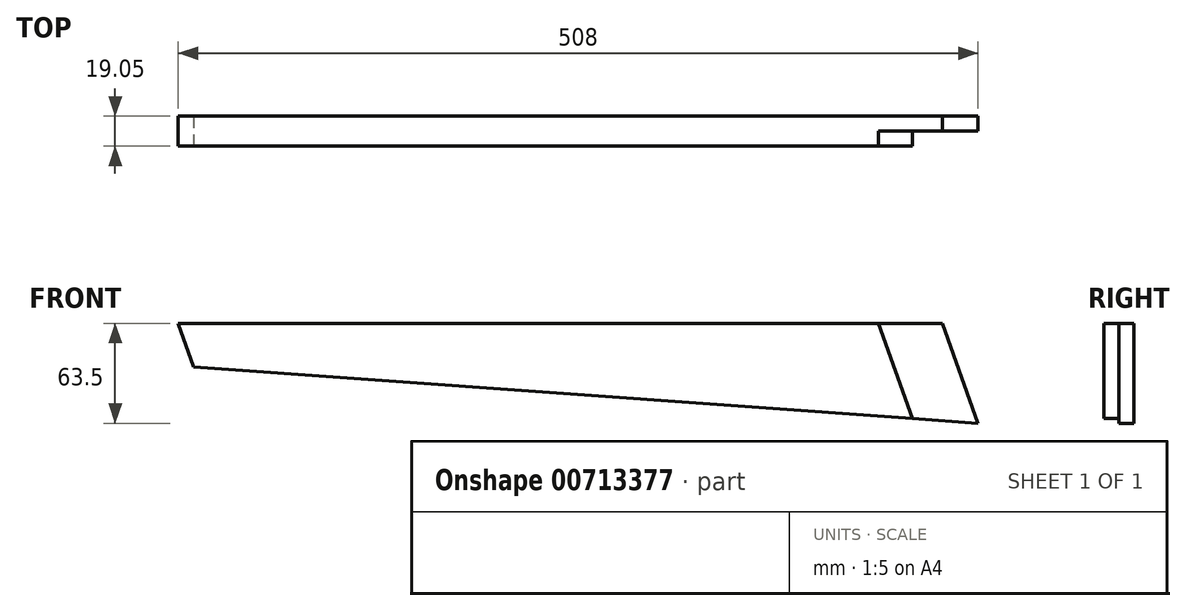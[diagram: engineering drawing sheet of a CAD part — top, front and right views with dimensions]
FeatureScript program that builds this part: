
annotation { "Feature Type Name" : "Feature", "Feature Type Description" : "" }
export const myFeature = defineFeature(function(context is Context, id is Id, definition is map)
    precondition{}
    {
        {
            var Q0;
            Q0=qCreatedBy(makeId("Front.planeOp"),FACE);
            var sketch = newSketch(context, id + "F0", { "sketchPlane" : qUnion([Q0])});
            skLineSegment(sketch, "E0.bottom", {"start": v(261.04, 0) * mm, "end": v(-246.96, 0) * mm});
            skLineSegment(sketch, "E0.top", {"start": v(261.04, 63.5) * mm, "end": v(-246.96, 63.5) * mm});
            skLineSegment(sketch, "E0.left", {"start": v(261.04, 0) * mm, "end": v(261.04, 63.5) * mm});
            skLineSegment(sketch, "E0.right", {"start": v(-246.96, 0) * mm, "end": v(-246.96, 63.5) * mm});
            skSolve(sketch);
        }
        {
            var Q0;
            Q0=qSketchRegion(id+"F0",true);
            extrude(context, id + "F1", {"entities" : qUnion([Q0]), "depth" : 19.05 * mm, "offsetDistance" : 25.4 * mm});
        }
        {
            var Q0;
            Q0=makeQuery(id+"F1.opExtrude","CAP_FACE",FACE,{"disambiguationData":[OSD([sQuery(id+"F0.wireOp",EDGE,"E0.bottom"),sQuery(id+"F0.wireOp",EDGE,"E0.top"),sQuery(id+"F0.wireOp",EDGE,"E0.left"),sQuery(id+"F0.wireOp",EDGE,"E0.right")])],"isStart":false});
            var sketch = newSketch(context, id + "F2", { "sketchPlane" : qUnion([Q0])});
            skLineSegment(sketch, "E1", {"start": v(-246.96, 63.5) * mm, "end": v(-224.26, 0) * mm});
            skLineSegment(sketch, "E2", {"start": v(-224.26, 0) * mm, "end": v(-246.96, 0) * mm});
            skLineSegment(sketch, "E3", {"start": v(-246.96, 0) * mm, "end": v(-246.96, 63.5) * mm});
            skSolve(sketch);
        }
        {
            var Q0;
            Q0=qSketchRegion(id+"F2",true);
            extrude(context, id + "F3", {"entities" : qUnion([Q0]), "operationType" : NewBodyOperationType.REMOVE, "oppositeDirection" : true, "depth" : 50.8 * mm, "offsetDistance" : 25.4 * mm});
        }
        {
            var Q0;
            Q0=makeQuery(id+"F1.opExtrude","CAP_FACE",FACE,{"disambiguationData":[OSD([sQuery(id+"F0.wireOp",EDGE,"E0.bottom"),sQuery(id+"F0.wireOp",EDGE,"E0.top"),sQuery(id+"F0.wireOp",EDGE,"E0.left"),sQuery(id+"F0.wireOp",EDGE,"E0.right")])],"isStart":false});
            var sketch = newSketch(context, id + "F4", { "sketchPlane" : qUnion([Q0])});
            skLineSegment(sketch, "E4", {"start": v(-237.09, 35.88) * mm, "end": v(261.04, 0) * mm});
            skLineSegment(sketch, "E5", {"start": v(261.04, 0) * mm, "end": v(-224.26, 0) * mm});
            skLineSegment(sketch, "E6", {"start": v(-224.26, 0) * mm, "end": v(-237.09, 35.88) * mm});
            skSolve(sketch);
        }
        {
            var Q0;
            Q0=qSketchRegion(id+"F4",true);
            extrude(context, id + "F5", {"entities" : qUnion([Q0]), "operationType" : NewBodyOperationType.REMOVE, "oppositeDirection" : true, "depth" : 50.8 * mm, "offsetDistance" : 25.4 * mm});
        }
        {
            var Q0;
            Q0=makeQuery(id+"F1.opExtrude","CAP_FACE",FACE,{"disambiguationData":[OSD([sQuery(id+"F0.wireOp",EDGE,"E0.bottom"),sQuery(id+"F0.wireOp",EDGE,"E0.top"),sQuery(id+"F0.wireOp",EDGE,"E0.left"),sQuery(id+"F0.wireOp",EDGE,"E0.right")])],"isStart":false});
            var sketch = newSketch(context, id + "F6", { "sketchPlane" : qUnion([Q0])});
            skLineSegment(sketch, "E7", {"start": v(261.04, 0) * mm, "end": v(238.33, 63.5) * mm});
            skLineSegment(sketch, "E8", {"start": v(238.33, 63.5) * mm, "end": v(261.04, 63.5) * mm});
            skLineSegment(sketch, "E9", {"start": v(261.04, 63.5) * mm, "end": v(261.04, 0) * mm});
            skSolve(sketch);
        }
        {
            var Q0;
            Q0=qSketchRegion(id+"F6",true);
            extrude(context, id + "F7", {"entities" : qUnion([Q0]), "operationType" : NewBodyOperationType.REMOVE, "oppositeDirection" : true, "depth" : 38.1 * mm, "offsetDistance" : 25.4 * mm});
        }
        {
            var Q0;
            Q0=makeQuery(id+"F7.boolean.opBoolean","COPY",FACE,{"derivedFrom":makeQuery(id+"F7.opExtrude","SWEPT_FACE",FACE,{"disambiguationData":[OSD([sQuery(id+"F6.wireOp",EDGE,"E7")])]})});
            var sketch = newSketch(context, id + "F8", { "sketchPlane" : qUnion([Q0])});
            skLineSegment(sketch, "E10", {"start": v(-19.05, -87.89) * mm, "end": v(-9.53, -87.89) * mm});
            skLineSegment(sketch, "E11", {"start": v(-19.05, -87.89) * mm, "end": v(-19.05, 40.52) * mm});
            skLineSegment(sketch, "E12", {"start": v(-9.52, 37.33) * mm, "end": v(-19.05, 40.52) * mm});
            skLineSegment(sketch, "E13", {"start": v(-9.53, -87.89) * mm, "end": v(-9.53, 37.33) * mm});
            skSolve(sketch);
        }
        {
            var Q0;
            Q0=qSketchRegion(id+"F8",true);
            extrude(context, id + "F9", {"entities" : qUnion([Q0]), "operationType" : NewBodyOperationType.REMOVE, "oppositeDirection" : true, "depth" : 38.1 * mm, "offsetDistance" : 25.4 * mm});
        }
    });
